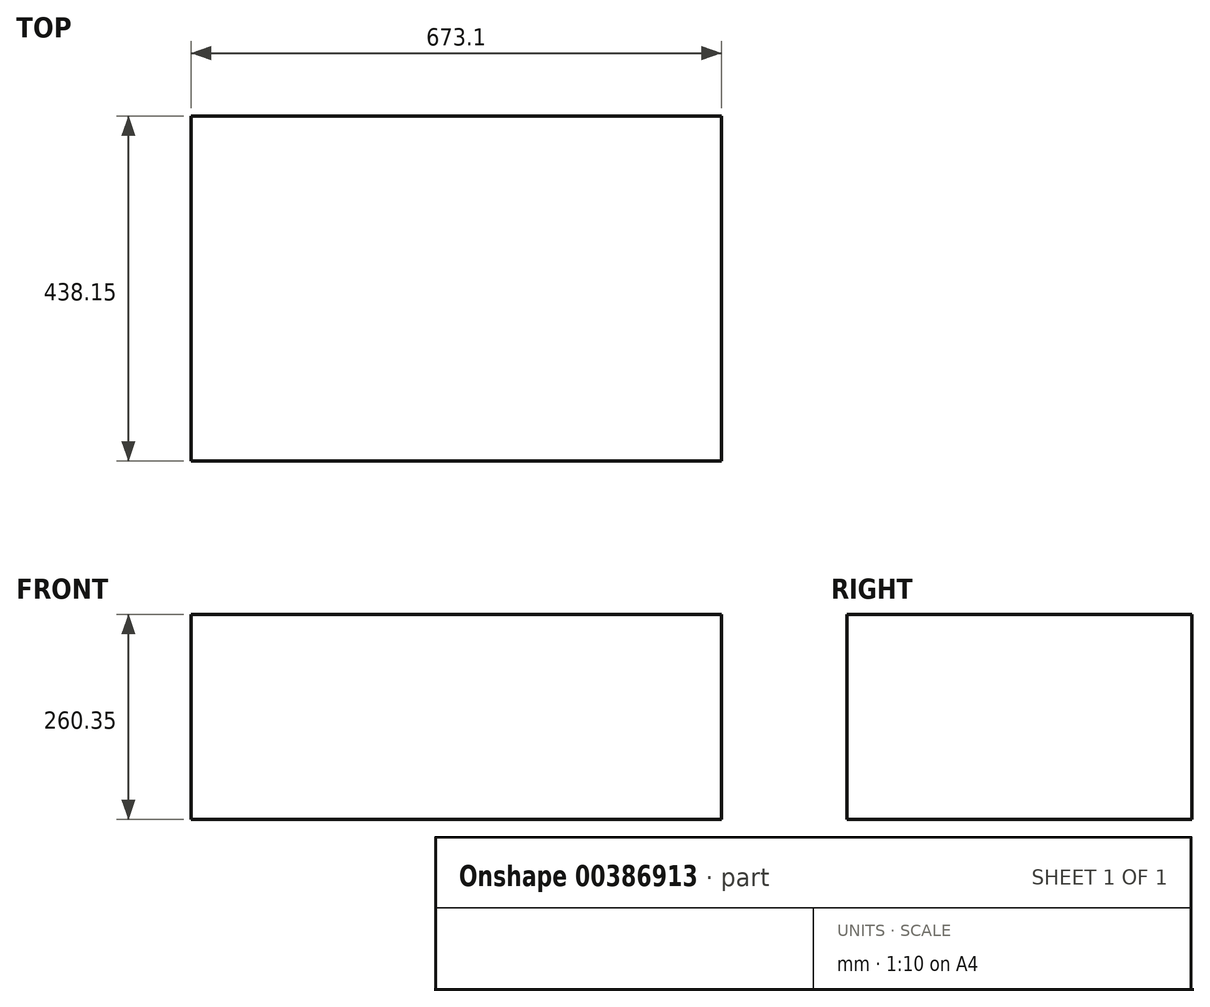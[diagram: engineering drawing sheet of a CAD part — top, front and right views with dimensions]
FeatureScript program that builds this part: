
annotation { "Feature Type Name" : "Feature", "Feature Type Description" : "" }
export const myFeature = defineFeature(function(context is Context, id is Id, definition is map)
    precondition{}
    {
        {
            var Q0;
            Q0=qCreatedBy(makeId("Front.planeOp"),FACE);
            var sketch = newSketch(context, id + "F0", { "sketchPlane" : qUnion([Q0])});
            skLineSegment(sketch, "E0.bottom", {"start": v(0, 0) * mm, "end": v(673.1, 0) * mm});
            skLineSegment(sketch, "E0.top", {"start": v(0, 260.35) * mm, "end": v(673.1, 260.35) * mm});
            skLineSegment(sketch, "E0.left", {"start": v(0, 0) * mm, "end": v(0, 260.35) * mm});
            skLineSegment(sketch, "E0.right", {"start": v(673.1, 0) * mm, "end": v(673.1, 260.35) * mm});
            skSolve(sketch);
        }
        {
            var Q0;
            Q0 = qSketchRegion(id + "F0", true);
            extrude(context, id + "F1", {"entities" : qUnion([Q0]), "oppositeDirection" : true, "depth" : 438.15 * mm});
        }
    });
